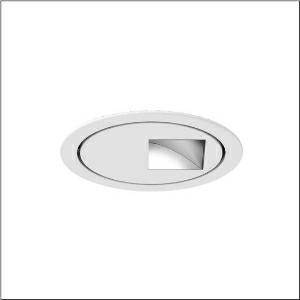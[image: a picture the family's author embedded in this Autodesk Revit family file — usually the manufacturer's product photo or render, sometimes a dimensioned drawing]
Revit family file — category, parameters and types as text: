
# Revit family: lunis_11_mini_round_51dk11cd2wm21
name_source: partatom
category: Lighting Fixtures
units: mm (PartAtom-declared; Revit-internal decimal feet)

## family parameters
Cut with Voids When Loaded = No
Host = Face
Light Source = No
Part Type = Normal
Room Calculation Point = No
Round Connector Dimension = Use Diameter
Shared = No

## types (1)
- Lunis 11 mini round (1 x LED 3000K / CRI = 90 (unbekannt), 1930 lm, 3000K)
    Apparent Load = 28 VA
    CIE Flux Codes = 44 77 97 100 100
    Color Rendering = 90
    Color Temperature = 3000K
    Default Elevation = 1800 mm
    Description = Lunis 11 mini round, downlight, light control with wallwasher, of highly reflective aluminium, highly specular, light emission: direct distribution, LED rated luminous flux: 1.930lm, light colour: 930, control gear: ECG, with terminal, 5-pole, mains connection: 220..230V, AC/DC, 0/50..60Hz, LED module, luminaire module, of aluminium, highly specular, white, diameter: 176mm, clamping range: 1..40mm, recessing ring, of plastic, traffic white (RAL 9016), protection rating (complete): IP20, insulation class (complete): insulation class II (safety insulation), certification: CE, permissible ambient temperature for indoor applications: 0..+35°C, packaging unit: 1 piece
    Height = 0 mm  [stored 0 ft]
    Lamp = 1 x LED 3000K / CRI >= 90 (unbekannt)
    Lamp Light Flux = 1930 lm
    Lamp count = 1
    Length = 176 mm
    Luminous efficacy = 69 lm/W
    Manufacturer = Siteco
    ModVariant = No
    Model = 51DK11CD2WM21
    Mounting Place = Ceiling
    Mounting Type = Recessed
    Number of Poles = 1
    OnlyDefault = Yes
    Power Factor = 1
    Product Name = Lunis 11 mini round
    Product group = downlight
    ProductGroupID = 401
    Protection Class = Protection class II
    Protection Degree = IP 20
    RLX_Detail_Level = 1
    RLX_Emergency_Light_Flux = 0 lm
    RLX_Emergency_Type = 0
    RLX_Emergency_Type_DB = No
    RlxData = <blob elided: 59245 chars, md5=291a1205>
    Socket = socket
    Standby Power = 0 W
    System Light Flux = 1930 lm
    System Power = 28 W
    Type Comments = Product without accessories
    Type Image = l_1004772.jpg
    URL = http://relux.com
    VarID = ---
    Voltage = 0 V
    Weight = 0.00 kg
    Width = 176 mm

note: [stored X ft] marks values corroborated as IEEE doubles in the binary element streams (Revit-internal decimal feet)

## geometry (parser evidence)
native form markers: Blend x4, Sweep x11
no freeform markers — native parametric forms only
